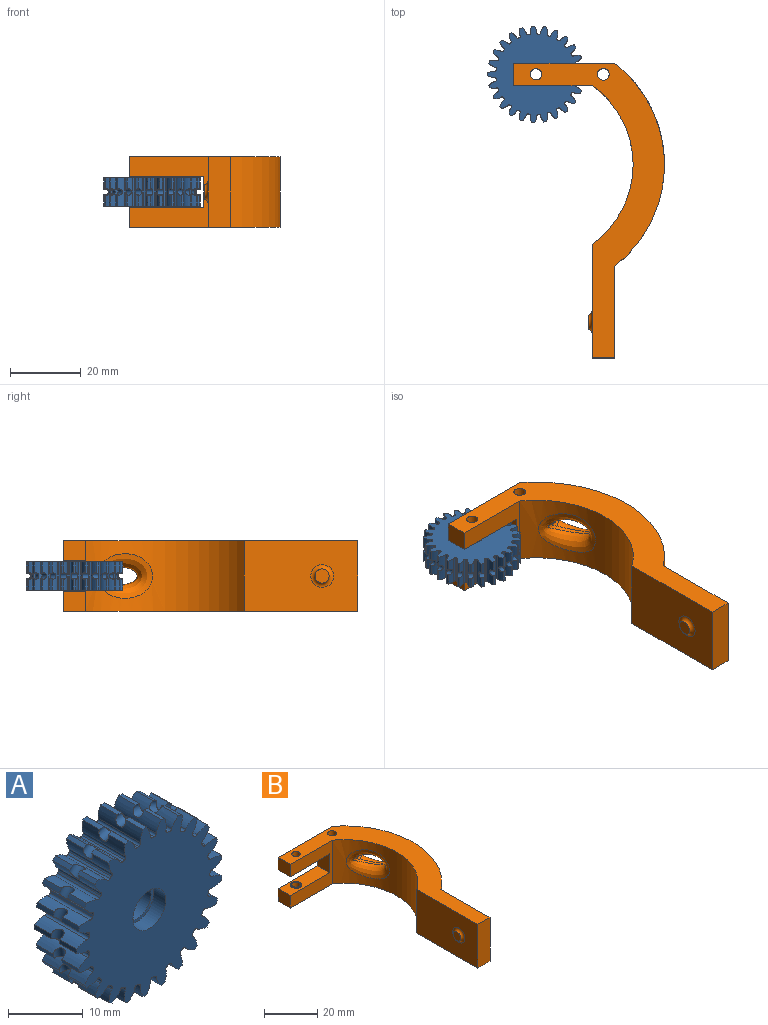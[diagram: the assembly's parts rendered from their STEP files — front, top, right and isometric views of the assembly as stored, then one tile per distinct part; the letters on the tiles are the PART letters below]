
ASSEMBLY  parts=2 mates=1
PART A: 207 faces, bbox 28x8x28 mm
  f0: cylinder r=2.6mm len=5.2mm, axis (0,1,0), area 56mm2, adj f204,f206
  f1: cylinder r=13.72mm len=3.21mm, axis (0,1,0), area 2.3mm2, adj f95,f100,f101,f178
  f2: cylinder r=13.72mm len=3.21mm, axis (0,1,0), area 2.3mm2, adj f95,f100,f102,f178
  f3: cylinder r=13.72mm len=3.21mm, axis (0,1,0), area 2.3mm2, adj f98,f99,f101,f179
  f4: cylinder r=13.72mm len=3.21mm, axis (0,1,0), area 2.3mm2, adj f98,f99,f102,f179
  f5: cylinder r=13.72mm len=3.21mm, axis (0,1,0), area 2.3mm2, adj f93,f96,f101,f181
  f6: cylinder r=13.72mm len=3.21mm, axis (0,1,0), area 2.3mm2, adj f93,f96,f102,f181
  f7: cylinder r=13.72mm len=3.21mm, axis (0,1,0), area 2.3mm2, adj f91,f94,f101,f182
  f8: cylinder r=13.72mm len=3.21mm, axis (0,1,0), area 2.3mm2, adj f91,f94,f102,f182
  f9: cylinder r=13.72mm len=3.21mm, axis (0,1,0), area 2.3mm2, adj f89,f92,f101,f183
  f10: cylinder r=13.72mm len=3.21mm, axis (0,1,0), area 2.3mm2, adj f89,f92,f102,f183
  f11: cylinder r=13.72mm len=3.21mm, axis (0,1,0), area 2.3mm2, adj f85,f90,f101,f184
  f12: cylinder r=13.72mm len=3.21mm, axis (0,1,0), area 2.3mm2, adj f85,f90,f102,f184
  f13: cylinder r=13.72mm len=3.21mm, axis (0,1,0), area 2.3mm2, adj f83,f88,f101,f185
  f14: cylinder r=13.72mm len=3.21mm, axis (0,1,0), area 2.3mm2, adj f83,f88,f102,f185
  f15: cylinder r=13.72mm len=3.21mm, axis (0,1,0), area 2.3mm2, adj f86,f87,f101,f186
  f16: cylinder r=13.72mm len=3.21mm, axis (0,1,0), area 2.3mm2, adj f86,f87,f102,f186
  f17: cylinder r=13.72mm len=3.21mm, axis (0,1,0), area 2.3mm2, adj f81,f84,f101,f187
  f18: cylinder r=13.72mm len=3.21mm, axis (0,1,0), area 2.3mm2, adj f81,f84,f102,f187
  f19: cylinder r=13.72mm len=3.21mm, axis (0,1,0), area 2.3mm2, adj f79,f82,f101,f188
  f20: cylinder r=13.72mm len=3.21mm, axis (0,1,0), area 2.3mm2, adj f79,f82,f102,f188
  f21: cylinder r=13.72mm len=3.21mm, axis (0,1,0), area 2.3mm2, adj f77,f80,f101,f189
  f22: cylinder r=13.72mm len=3.21mm, axis (0,1,0), area 2.3mm2, adj f77,f80,f102,f189
  f23: cylinder r=13.72mm len=3.21mm, axis (0,1,0), area 2.3mm2, adj f71,f78,f101,f190
  f24: cylinder r=13.72mm len=3.21mm, axis (0,1,0), area 2.3mm2, adj f71,f78,f102,f190
  f25: cylinder r=13.72mm len=3.21mm, axis (0,1,0), area 2.3mm2, adj f51,f76,f101,f191
  f26: cylinder r=13.72mm len=3.21mm, axis (0,1,0), area 2.3mm2, adj f51,f76,f102,f191
  f27: cylinder r=13.72mm len=3.21mm, axis (0,1,0), area 2.3mm2, adj f74,f75,f101,f192
  f28: cylinder r=13.72mm len=3.21mm, axis (0,1,0), area 2.3mm2, adj f74,f75,f102,f192
  f29: cylinder r=13.72mm len=3.21mm, axis (0,1,0), area 2.3mm2, adj f69,f72,f101,f194
  f30: cylinder r=13.72mm len=3.21mm, axis (0,1,0), area 2.3mm2, adj f69,f72,f102,f194
  f31: cylinder r=13.72mm len=3.21mm, axis (0,1,0), area 2.3mm2, adj f70,f73,f101,f193
  f32: cylinder r=13.72mm len=3.21mm, axis (0,1,0), area 2.3mm2, adj f70,f73,f102,f193
  f33: cylinder r=13.72mm len=3.21mm, axis (0,1,0), area 2.3mm2, adj f68,f97,f101,f180
  f34: cylinder r=13.72mm len=3.21mm, axis (0,1,0), area 2.3mm2, adj f68,f97,f102,f180
  f35: cylinder r=13.72mm len=3.21mm, axis (0,1,0), area 2.3mm2, adj f66,f67,f101,f195
  f36: cylinder r=13.72mm len=3.21mm, axis (0,1,0), area 2.3mm2, adj f66,f67,f102,f195
  f37: cylinder r=13.72mm len=3.21mm, axis (0,1,0), area 2.3mm2, adj f64,f65,f101,f196
  f38: cylinder r=13.72mm len=3.21mm, axis (0,1,0), area 2.3mm2, adj f64,f65,f102,f196
  f39: cylinder r=13.72mm len=3.21mm, axis (0,1,0), area 2.3mm2, adj f62,f63,f101,f197
  f40: cylinder r=13.72mm len=3.21mm, axis (0,1,0), area 2.3mm2, adj f62,f63,f102,f197
  f41: cylinder r=13.72mm len=3.21mm, axis (0,1,0), area 2.3mm2, adj f57,f60,f101,f199
  f42: cylinder r=13.72mm len=3.21mm, axis (0,1,0), area 2.3mm2, adj f57,f60,f102,f199
  f43: cylinder r=13.72mm len=3.21mm, axis (0,1,0), area 2.3mm2, adj f53,f58,f101,f201
  f44: cylinder r=13.72mm len=3.21mm, axis (0,1,0), area 2.3mm2, adj f53,f58,f102,f201
  f45: cylinder r=13.72mm len=3.21mm, axis (0,1,0), area 2.3mm2, adj f56,f61,f101,f198
  f46: cylinder r=13.72mm len=3.21mm, axis (0,1,0), area 2.3mm2, adj f56,f61,f102,f198
  f47: cylinder r=13.72mm len=3.21mm, axis (0,1,0), area 2.3mm2, adj f54,f55,f101,f202
  f48: cylinder r=13.72mm len=3.21mm, axis (0,1,0), area 2.3mm2, adj f54,f55,f102,f202
  f49: cylinder r=13.72mm len=3.21mm, axis (0,1,0), area 2.3mm2, adj f52,f59,f101,f200
  f50: cylinder r=13.72mm len=3.21mm, axis (0,1,0), area 2.3mm2, adj f52,f59,f102,f200
  f51: extruded ~8x1.85mm, area 14.3mm2, adj f25,f26,f101,f102,f104,f191
  f52: extruded ~8x1.85mm, area 14.3mm2, adj f49,f50,f101,f102,f105,f200
  f53: extruded ~8x1.89mm, area 14.3mm2, adj f43,f44,f101,f102,f107,f201
  f54: extruded ~8x1.85mm, area 14.3mm2, adj f47,f48,f101,f102,f108,f202
  f55: extruded ~8x1.66mm, area 14.3mm2, adj f47,f48,f101,f102,f110,f202
  f56: extruded ~8x1.99mm, area 14.3mm2, adj f45,f46,f101,f102,f111,f198
  f57: extruded ~8x2.01mm, area 14.3mm2, adj f41,f42,f101,f102,f113,f199
  f58: extruded ~8x1.59mm, area 14.3mm2, adj f43,f44,f101,f102,f114,f201
  f59: extruded ~8x1.99mm, area 14.3mm2, adj f49,f50,f101,f102,f116,f200
  f60: extruded ~8x1.6mm, area 14.3mm2, adj f41,f42,f101,f102,f117,f199
  f61: extruded ~8x1.52mm, area 14.3mm2, adj f45,f46,f101,f102,f119,f198
  f62: extruded ~8x2.01mm, area 14.3mm2, adj f39,f40,f101,f102,f120,f197
  f63: extruded ~8x1.8mm, area 14.3mm2, adj f39,f40,f101,f102,f122,f197
  f64: extruded ~8x1.9mm, area 14.3mm2, adj f37,f38,f101,f102,f123,f196
  f65: extruded ~8x1.97mm, area 14.3mm2, adj f37,f38,f101,f102,f125,f196
  f66: extruded ~8x1.67mm, area 14.3mm2, adj f35,f36,f101,f102,f126,f195
  f67: extruded ~8x2.02mm, area 14.3mm2, adj f35,f36,f101,f102,f128,f195
  f68: extruded ~8x1.51mm, area 14.3mm2, adj f33,f34,f101,f102,f129,f180
  f69: extruded ~8x1.85mm, area 14.3mm2, adj f29,f30,f101,f102,f131,f194
  f70: extruded ~8x1.89mm, area 14.3mm2, adj f31,f32,f101,f102,f132,f193
  f71: extruded ~8x1.99mm, area 14.3mm2, adj f23,f24,f101,f102,f134,f190
  f72: extruded ~8x1.66mm, area 14.3mm2, adj f29,f30,f101,f102,f135,f194
  f73: extruded ~8x1.59mm, area 14.3mm2, adj f31,f32,f101,f102,f137,f193
  f74: extruded ~8x2.01mm, area 14.3mm2, adj f27,f28,f101,f102,f138,f192
  f75: extruded ~8x1.6mm, area 14.3mm2, adj f27,f28,f101,f102,f140,f192
  f76: extruded ~8x1.99mm, area 14.3mm2, adj f25,f26,f101,f102,f141,f191
  f77: extruded ~8x2.01mm, area 14.3mm2, adj f21,f22,f101,f102,f143,f189
  f78: extruded ~8x1.52mm, area 14.3mm2, adj f23,f24,f101,f102,f144,f190
  f79: extruded ~8x1.9mm, area 14.3mm2, adj f19,f20,f101,f102,f146,f188
  f80: extruded ~8x1.8mm, area 14.3mm2, adj f21,f22,f101,f102,f147,f189
  f81: extruded ~8x1.67mm, area 14.3mm2, adj f17,f18,f101,f102,f149,f187
  f82: extruded ~8x1.97mm, area 14.3mm2, adj f19,f20,f101,f102,f150,f188
  f83: extruded ~8x1.51mm, area 14.3mm2, adj f13,f14,f101,f102,f152,f185
  f84: extruded ~8x2.02mm, area 14.3mm2, adj f17,f18,f101,f102,f153,f187
  f85: extruded ~8x1.97mm, area 14.3mm2, adj f11,f12,f101,f102,f155,f184
  f86: extruded ~8x1.73mm, area 14.3mm2, adj f15,f16,f101,f102,f156,f186
  f87: extruded ~8x1.79mm, area 14.3mm2, adj f15,f16,f101,f102,f158,f186
  f88: extruded ~8x1.93mm, area 14.3mm2, adj f13,f14,f101,f102,f159,f185
  f89: extruded ~8x2.02mm, area 14.3mm2, adj f9,f10,f101,f102,f161,f183
  f90: extruded ~8x1.43mm, area 14.3mm2, adj f11,f12,f101,f102,f162,f184
  f91: extruded ~8x1.94mm, area 14.3mm2, adj f7,f8,f101,f102,f164,f182
  f92: extruded ~8x1.74mm, area 14.3mm2, adj f9,f10,f101,f102,f165,f183
  f93: extruded ~8x1.74mm, area 14.3mm2, adj f5,f6,f101,f102,f167,f181
  f94: extruded ~8x1.94mm, area 14.3mm2, adj f7,f8,f101,f102,f168,f182
  f95: extruded ~8x1.43mm, area 14.3mm2, adj f1,f2,f101,f102,f170,f178
  f96: extruded ~8x2.02mm, area 14.3mm2, adj f5,f6,f101,f102,f171,f181
  f97: extruded ~8x1.93mm, area 14.3mm2, adj f33,f34,f101,f102,f173,f180
  f98: extruded ~8x1.79mm, area 14.3mm2, adj f3,f4,f101,f102,f174,f179
  f99: extruded ~8x1.73mm, area 14.3mm2, adj f3,f4,f101,f102,f176,f179
  f100: extruded ~8x1.97mm, area 14.3mm2, adj f1,f2,f101,f102,f177,f178
  f101: plane 27.42x27.37mm, normal (0,-1,0), area 469mm2, adj f1,f3,f5,f7,f9,f11,f13,f15
  f102: plane 27.42x27.37mm, normal (0,1,0), area 469mm2, adj f2,f4,f6,f8,f10,f12,f14,f16
  f103: cylinder r=11.43mm len=8mm, axis (0,1,0), area 2.8mm2, adj f101,f102,f104,f105
  f104: cylinder r=0.38mm len=8mm, axis (0,1,0), area 4.7mm2, adj f51,f101,f102,f103
  f105: cylinder r=0.38mm len=8mm, axis (0,1,0), area 4.7mm2, adj f52,f101,f102,f103
  f106: cylinder r=11.43mm len=8mm, axis (0,1,0), area 2.8mm2, adj f101,f102,f107,f108
  f107: cylinder r=0.38mm len=8mm, axis (0,1,0), area 4.7mm2, adj f53,f101,f102,f106
  f108: cylinder r=0.38mm len=8mm, axis (0,1,0), area 4.7mm2, adj f54,f101,f102,f106
  f109: cylinder r=11.43mm len=8mm, axis (0,1,0), area 2.8mm2, adj f101,f102,f110,f111
  f110: cylinder r=0.38mm len=8mm, axis (0,1,0), area 4.7mm2, adj f55,f101,f102,f109
  f111: cylinder r=0.38mm len=8mm, axis (0,1,0), area 4.7mm2, adj f56,f101,f102,f109
  f112: cylinder r=11.43mm len=8mm, axis (0,1,0), area 2.8mm2, adj f101,f102,f113,f114
  f113: cylinder r=0.38mm len=8mm, axis (0,1,0), area 4.7mm2, adj f57,f101,f102,f112
  f114: cylinder r=0.38mm len=8mm, axis (0,1,0), area 4.7mm2, adj f58,f101,f102,f112
  f115: cylinder r=11.43mm len=8mm, axis (0,1,0), area 2.8mm2, adj f101,f102,f116,f117
  f116: cylinder r=0.38mm len=8mm, axis (0,1,0), area 4.7mm2, adj f59,f101,f102,f115
  f117: cylinder r=0.38mm len=8mm, axis (0,1,0), area 4.7mm2, adj f60,f101,f102,f115
  f118: cylinder r=11.43mm len=8mm, axis (0,1,0), area 2.8mm2, adj f101,f102,f119,f120
  f119: cylinder r=0.38mm len=8mm, axis (0,1,0), area 4.7mm2, adj f61,f101,f102,f118
  f120: cylinder r=0.38mm len=8mm, axis (0,1,0), area 4.7mm2, adj f62,f101,f102,f118
  f121: cylinder r=11.43mm len=8mm, axis (0,1,0), area 2.8mm2, adj f101,f102,f122,f123
  f122: cylinder r=0.38mm len=8mm, axis (0,1,0), area 4.7mm2, adj f63,f101,f102,f121
  f123: cylinder r=0.38mm len=8mm, axis (0,1,0), area 4.7mm2, adj f64,f101,f102,f121
  f124: cylinder r=11.43mm len=8mm, axis (0,1,0), area 2.8mm2, adj f101,f102,f125,f126
  f125: cylinder r=0.38mm len=8mm, axis (0,1,0), area 4.7mm2, adj f65,f101,f102,f124
  f126: cylinder r=0.38mm len=8mm, axis (0,1,0), area 4.7mm2, adj f66,f101,f102,f124
  f127: cylinder r=11.43mm len=8mm, axis (0,1,0), area 2.8mm2, adj f101,f102,f128,f129
  f128: cylinder r=0.38mm len=8mm, axis (0,1,0), area 4.7mm2, adj f67,f101,f102,f127
  f129: cylinder r=0.38mm len=8mm, axis (0,1,0), area 4.7mm2, adj f68,f101,f102,f127
  f130: cylinder r=11.43mm len=8mm, axis (0,1,0), area 2.8mm2, adj f101,f102,f131,f132
  f131: cylinder r=0.38mm len=8mm, axis (0,1,0), area 4.7mm2, adj f69,f101,f102,f130
  f132: cylinder r=0.38mm len=8mm, axis (0,1,0), area 4.7mm2, adj f70,f101,f102,f130
  f133: cylinder r=11.43mm len=8mm, axis (0,1,0), area 2.8mm2, adj f101,f102,f134,f135
  f134: cylinder r=0.38mm len=8mm, axis (0,1,0), area 4.7mm2, adj f71,f101,f102,f133
  f135: cylinder r=0.38mm len=8mm, axis (0,1,0), area 4.7mm2, adj f72,f101,f102,f133
  f136: cylinder r=11.43mm len=8mm, axis (0,1,0), area 2.8mm2, adj f101,f102,f137,f138
  f137: cylinder r=0.38mm len=8mm, axis (0,1,0), area 4.7mm2, adj f73,f101,f102,f136
  f138: cylinder r=0.38mm len=8mm, axis (0,1,0), area 4.7mm2, adj f74,f101,f102,f136
  f139: cylinder r=11.43mm len=8mm, axis (0,1,0), area 2.8mm2, adj f101,f102,f140,f141
  f140: cylinder r=0.38mm len=8mm, axis (0,1,0), area 4.7mm2, adj f75,f101,f102,f139
  f141: cylinder r=0.38mm len=8mm, axis (0,1,0), area 4.7mm2, adj f76,f101,f102,f139
  f142: cylinder r=11.43mm len=8mm, axis (0,1,0), area 2.8mm2, adj f101,f102,f143,f144
  f143: cylinder r=0.38mm len=8mm, axis (0,1,0), area 4.7mm2, adj f77,f101,f102,f142
  f144: cylinder r=0.38mm len=8mm, axis (0,1,0), area 4.7mm2, adj f78,f101,f102,f142
  f145: cylinder r=11.43mm len=8mm, axis (0,1,0), area 2.8mm2, adj f101,f102,f146,f147
  f146: cylinder r=0.38mm len=8mm, axis (0,1,0), area 4.7mm2, adj f79,f101,f102,f145
  f147: cylinder r=0.38mm len=8mm, axis (0,1,0), area 4.7mm2, adj f80,f101,f102,f145
  f148: cylinder r=11.43mm len=8mm, axis (0,1,0), area 2.8mm2, adj f101,f102,f149,f150
  f149: cylinder r=0.38mm len=8mm, axis (0,1,0), area 4.7mm2, adj f81,f101,f102,f148
  f150: cylinder r=0.38mm len=8mm, axis (0,1,0), area 4.7mm2, adj f82,f101,f102,f148
  f151: cylinder r=11.43mm len=8mm, axis (0,1,0), area 2.8mm2, adj f101,f102,f152,f153
  f152: cylinder r=0.38mm len=8mm, axis (0,1,0), area 4.7mm2, adj f83,f101,f102,f151
  f153: cylinder r=0.38mm len=8mm, axis (0,1,0), area 4.7mm2, adj f84,f101,f102,f151
  f154: cylinder r=11.43mm len=8mm, axis (0,1,0), area 2.8mm2, adj f101,f102,f155,f156
  f155: cylinder r=0.38mm len=8mm, axis (0,1,0), area 4.7mm2, adj f85,f101,f102,f154
  f156: cylinder r=0.38mm len=8mm, axis (0,1,0), area 4.7mm2, adj f86,f101,f102,f154
  f157: cylinder r=11.43mm len=8mm, axis (0,1,0), area 2.8mm2, adj f101,f102,f158,f159
  f158: cylinder r=0.38mm len=8mm, axis (0,1,0), area 4.7mm2, adj f87,f101,f102,f157
  f159: cylinder r=0.38mm len=8mm, axis (0,1,0), area 4.7mm2, adj f88,f101,f102,f157
  f160: cylinder r=11.43mm len=8mm, axis (0,1,0), area 2.8mm2, adj f101,f102,f161,f162
  f161: cylinder r=0.38mm len=8mm, axis (0,1,0), area 4.7mm2, adj f89,f101,f102,f160
  f162: cylinder r=0.38mm len=8mm, axis (0,1,0), area 4.7mm2, adj f90,f101,f102,f160
  f163: cylinder r=11.43mm len=8mm, axis (0,1,0), area 2.8mm2, adj f101,f102,f164,f165
  f164: cylinder r=0.38mm len=8mm, axis (0,1,0), area 4.7mm2, adj f91,f101,f102,f163
  f165: cylinder r=0.38mm len=8mm, axis (0,1,0), area 4.7mm2, adj f92,f101,f102,f163
  f166: cylinder r=11.43mm len=8mm, axis (0,1,0), area 2.8mm2, adj f101,f102,f167,f168
  f167: cylinder r=0.38mm len=8mm, axis (0,1,0), area 4.7mm2, adj f93,f101,f102,f166
  f168: cylinder r=0.38mm len=8mm, axis (0,1,0), area 4.7mm2, adj f94,f101,f102,f166
  f169: cylinder r=11.43mm len=8mm, axis (0,1,0), area 2.8mm2, adj f101,f102,f170,f171
  f170: cylinder r=0.38mm len=8mm, axis (0,1,0), area 4.7mm2, adj f95,f101,f102,f169
  f171: cylinder r=0.38mm len=8mm, axis (0,1,0), area 4.7mm2, adj f96,f101,f102,f169
  f172: cylinder r=11.43mm len=8mm, axis (0,1,0), area 2.8mm2, adj f101,f102,f173,f174
  f173: cylinder r=0.38mm len=8mm, axis (0,1,0), area 4.7mm2, adj f97,f101,f102,f172
  f174: cylinder r=0.38mm len=8mm, axis (0,1,0), area 4.7mm2, adj f98,f101,f102,f172
  f175: cylinder r=11.43mm len=8mm, axis (0,1,0), area 2.8mm2, adj f101,f102,f176,f177
  f176: cylinder r=0.38mm len=8mm, axis (0,1,0), area 4.7mm2, adj f99,f101,f102,f175
  f177: cylinder r=0.38mm len=8mm, axis (0,1,0), area 4.7mm2, adj f100,f101,f102,f175
  f178: torus R=13.33mm, axis (0,-1,0), area 4.9mm2, adj f1,f2,f95,f100
  f179: torus R=13.33mm, axis (0,-1,0), area 4.9mm2, adj f3,f4,f98,f99
  f180: torus R=13.33mm, axis (0,-1,0), area 4.9mm2, adj f33,f34,f68,f97
  f181: torus R=13.33mm, axis (0,-1,0), area 4.9mm2, adj f5,f6,f93,f96
  f182: torus R=13.33mm, axis (0,-1,0), area 4.9mm2, adj f7,f8,f91,f94
  f183: torus R=13.33mm, axis (0,-1,0), area 4.9mm2, adj f9,f10,f89,f92
  f184: torus R=13.33mm, axis (0,-1,0), area 4.9mm2, adj f11,f12,f85,f90
  f185: torus R=13.33mm, axis (0,-1,0), area 4.9mm2, adj f13,f14,f83,f88
  f186: torus R=13.33mm, axis (0,-1,0), area 4.9mm2, adj f15,f16,f86,f87
  f187: torus R=13.33mm, axis (0,-1,0), area 4.9mm2, adj f17,f18,f81,f84
  f188: torus R=13.33mm, axis (0,-1,0), area 4.9mm2, adj f19,f20,f79,f82
  f189: torus R=13.33mm, axis (0,-1,0), area 4.9mm2, adj f21,f22,f77,f80
  f190: torus R=13.33mm, axis (0,-1,0), area 4.9mm2, adj f23,f24,f71,f78
  f191: torus R=13.33mm, axis (0,-1,0), area 4.9mm2, adj f25,f26,f51,f76
  f192: torus R=13.33mm, axis (0,-1,0), area 4.9mm2, adj f27,f28,f74,f75
  f193: torus R=13.33mm, axis (0,-1,0), area 4.9mm2, adj f31,f32,f70,f73
  f194: torus R=13.33mm, axis (0,-1,0), area 4.9mm2, adj f29,f30,f69,f72
  f195: torus R=13.33mm, axis (0,-1,0), area 4.9mm2, adj f35,f36,f66,f67
  f196: torus R=13.33mm, axis (0,-1,0), area 4.9mm2, adj f37,f38,f64,f65
  f197: torus R=13.33mm, axis (0,-1,0), area 4.9mm2, adj f39,f40,f62,f63
  f198: torus R=13.33mm, axis (0,-1,0), area 4.9mm2, adj f45,f46,f56,f61
  f199: torus R=13.33mm, axis (0,-1,0), area 4.9mm2, adj f41,f42,f57,f60
  f200: torus R=13.33mm, axis (0,-1,0), area 4.9mm2, adj f49,f50,f52,f59
  f201: torus R=13.33mm, axis (0,-1,0), area 4.9mm2, adj f43,f44,f53,f58
  f202: torus R=13.33mm, axis (0,-1,0), area 4.9mm2, adj f47,f48,f54,f55
  f203: cylinder r=3.1mm len=6.2mm, axis (0,-1,0), area 44.5mm2, adj f101,f204
  f204: plane 6.2x6.2mm, normal (0,-1,0), area 9mm2, adj f0,f203
  f205: cylinder r=3.1mm len=6.2mm, axis (0,1,0), area 44.5mm2, adj f102,f206
  f206: plane 6.2x6.2mm, normal (0,1,0), area 9mm2, adj f0,f205
PART B: 28 faces, bbox 42.8x83.6x20 mm
  f0: bspline ~8.48x6.78mm, area 15.3mm2, adj f1,f3,f21,f23
  f1: bspline ~8.48x6.77mm, area 15.1mm2, adj f0,f3,f21,f23
  f2: cylinder r=27.52mm len=44.96mm, axis (0,0,1), area 878.2mm2, adj f4,f6,f8,f20,f22
  f3: cylinder r=36.4mm len=57.66mm, axis (0,0,1), area 1114.6mm2, adj f0,f1,f5,f6,f8,f16,f23
  f4: plane 32.28x20mm, normal (-1,0,0), area 612.6mm2, adj f2,f6,f7,f8,f10
  f5: plane 25.93x20mm, normal (1,0,0), area 518.6mm2, adj f3,f6,f7,f8
  f6: plane 83.59x42.75mm, normal (0,0,1), area 858.5mm2, adj f2,f3,f4,f5,f7,f14,f15,f16
  f7: plane 20x6.35mm, normal (0,-1,0), area 127mm2, adj f4,f5,f6,f8
  f8: plane 83.59x42.75mm, normal (0,0,-1), area 858.5mm2, adj f2,f3,f4,f5,f7,f16,f17,f18
  f9: plane 4x4mm, normal (-1,0,0), area 12.6mm2, adj f10
  f10: torus R=3.24mm, axis (1,0,0), area 27.1mm2, adj f4,f9
  f11: plane 8.6x6.35mm, normal (-1,0,0), area 54.6mm2, adj f12,f13,f16,f20
  f12: plane 21x6.35mm, normal (0,0,-1), area 120.8mm2, adj f11,f15,f16,f20,f26
  f13: plane 21x6.35mm, normal (0,0,1), area 120.8mm2, adj f11,f16,f17,f20,f24
  f14: cylinder r=1.6mm len=6mm, axis (0,0,1), area 60.3mm2, adj f6,f27
  f15: plane 6.35x5.7mm, normal (-1,0,0), area 36.2mm2, adj f6,f12,f16,f20
  f16: plane 28.58x20mm, normal (0,1,0), area 390.9mm2, adj f3,f6,f8,f11,f12,f13,f15,f17
  f17: plane 6.35x5.7mm, normal (-1,0,0), area 36.2mm2, adj f8,f13,f16,f20
  f18: cylinder r=1.6mm len=6mm, axis (0,0,1), area 60.3mm2, adj f8,f25
  f19: cylinder r=1.66mm len=20mm, axis (0,0,1), area 209.2mm2, adj f6,f8
  f20: plane 22.23x20mm, normal (0,-1,0), area 263.9mm2, adj f2,f6,f8,f11,f12,f13,f15,f17
  f21: extruded ~10x9.69mm, area 34.3mm2, adj f0,f1,f22,f23
  f22: bspline ~15.49x12.64mm, area 192.9mm2, adj f2,f21
  f23: bspline ~18.6x12.62mm, area 211.3mm2, adj f0,f1,f3,f21
  f24: cylinder r=2mm len=4mm, axis (0,0,-1), area 3.8mm2, adj f13,f25
  f25: plane 4x4mm, normal (0,0,1), area 4.5mm2, adj f18,f24
  f26: cylinder r=2mm len=4mm, axis (0,0,1), area 3.8mm2, adj f12,f27
  f27: plane 4x4mm, normal (0,0,-1), area 4.5mm2, adj f14,f26
PLACE A rot(axis=(1,0,0),90deg) t=(-19.05,0,14)mm
PLACE B at identity fixed
MATE revolute A.f0 <-> B.f24  axis (0,0,1) through (-19.05,0,10)mm
